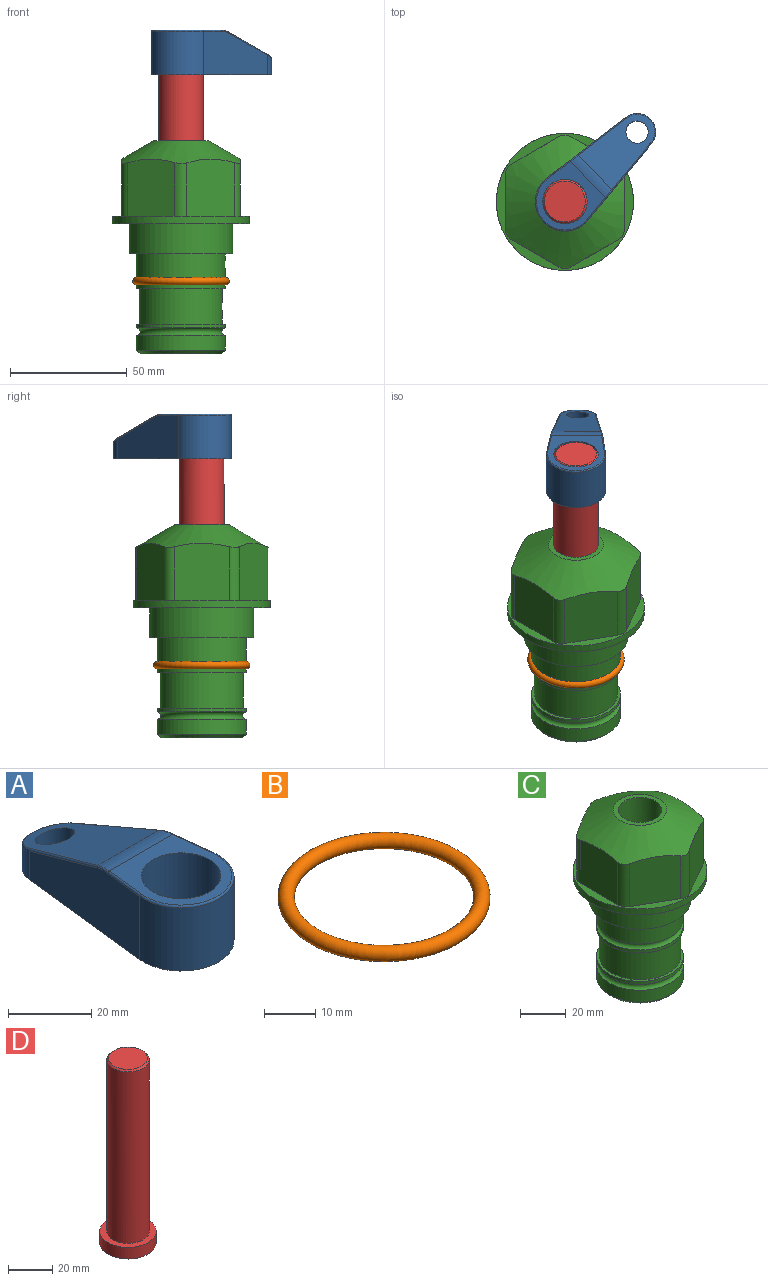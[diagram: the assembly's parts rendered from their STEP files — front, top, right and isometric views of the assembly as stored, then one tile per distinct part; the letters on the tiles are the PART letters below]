
ASSEMBLY  parts=4 mates=2
PART A: 44 faces, bbox 27.5x64.5x19.1 mm
  f0: plane 2.3x0.95mm, normal (0,0,-1), area 1mm2, adj f25,f30,f34
  f1: plane 63.5x25.4mm, normal (0,0,-1), area 561.7mm2, adj f2,f3,f4,f5,f6,f7,f19,f20
  f2: cylinder r=12.7mm len=25.4mm, axis (0,0,-1), area 792.2mm2, adj f1,f3,f5,f13
  f3: plane 42.33x18.54mm, normal (0.99,0.11,0), area 647mm2, adj f1,f2,f4,f11,f12,f14
  f4: cylinder r=7.94mm len=15.78mm, axis (0,0,-1), area 158.6mm2, adj f1,f3,f5,f16
  f5: plane 42.33x18.54mm, normal (-0.99,0.11,0), area 647mm2, adj f1,f2,f4,f15,f17,f18
  f6: cylinder r=9.53mm len=19.05mm, axis (0,0,-1), area 1140.1mm2, adj f1,f8
  f7: cylinder r=4.76mm len=10.98mm, axis (0,0,-1), area 276.1mm2, adj f1,f9
  f8: plane 25.83x24.38mm, normal (0,0,1), area 262.2mm2, adj f6,f10,f11,f13,f15
  f9: plane 32.49x20.55mm, normal (0,0.34,0.94), area 489.9mm2, adj f7,f10,f14,f16,f18
  f10: cylinder r=12.7mm len=21.49mm, axis (-1,0,0), area 93.2mm2, adj f8,f9,f12,f17
  f11: cylinder r=0.51mm len=12.34mm, axis (0.11,-0.99,0), area 9.9mm2, adj f3,f8,f12,f13
  f12: bspline ~7.62x1.64mm, area 3.5mm2, adj f3,f10,f11,f14
  f13: torus R=12.19mm, axis (0,0,1), area 33.6mm2, adj f2,f8,f11,f15
  f14: cylinder r=0.51mm len=26.01mm, axis (0.1,-0.93,0.34), area 21.6mm2, adj f3,f9,f12,f16
  f15: cylinder r=0.51mm len=12.34mm, axis (0.11,0.99,0), area 9.9mm2, adj f5,f8,f13,f17
  f16: bspline ~15.78x7.05mm, area 15.7mm2, adj f4,f9,f14,f18
  f17: bspline ~7.62x1.64mm, area 3.5mm2, adj f5,f10,f15,f18
  f18: cylinder r=0.51mm len=26.01mm, axis (0.1,0.93,-0.34), area 21.6mm2, adj f5,f9,f16,f17
  f19: plane 21.6x14.29mm, normal (-0.99,-0.11,0), area 242.6mm2, adj f1,f26,f28,f34,f36,f38
  f20: plane 21.6x14.29mm, normal (0.99,-0.11,0), area 242.6mm2, adj f1,f27,f29,f37,f39,f41
  f21: cylinder r=12.7mm len=14.29mm, axis (0,0,-1), area 173.2mm2, adj f1,f26,f27,f30,f31,f33
  f22: cylinder r=7.94mm len=7.63mm, axis (0,0,-1), area 53.8mm2, adj f1,f28,f29,f42
  f23: plane 2.3x0.95mm, normal (0,0,-1), area 1mm2, adj f25,f33,f37
  f24: plane 17.94x12.32mm, normal (0,-0.34,-0.94), area 191.2mm2, adj f25,f38,f41,f42
  f25: cylinder r=9.53mm len=12.93mm, axis (-1,0,0), area 37.5mm2, adj f0,f23,f24,f31,f36,f39
  f26: cylinder r=1.59mm len=14.29mm, axis (0,0,-1), area 49mm2, adj f1,f19,f21,f32
  f27: cylinder r=1.59mm len=14.29mm, axis (0,0,-1), area 49mm2, adj f1,f20,f21,f35
  f28: cylinder r=1.59mm len=7.28mm, axis (0,0,-1), area 22.1mm2, adj f1,f19,f22,f40
  f29: cylinder r=1.59mm len=7.28mm, axis (0,0,-1), area 22.1mm2, adj f1,f20,f22,f43
  f30: torus R=14.29mm, axis (0,0,1), area 5.8mm2, adj f0,f21,f31,f32
  f31: bspline ~11.06x2.73mm, area 20.8mm2, adj f21,f25,f30,f33
  f32: sphere r=1.59mm, area 5.4mm2, adj f26,f30,f34
  f33: torus R=14.29mm, axis (0,0,1), area 5.8mm2, adj f21,f23,f31,f35
  f34: cylinder r=1.59mm len=1.68mm, axis (-0.11,0.99,0), area 2.4mm2, adj f0,f19,f32,f36
  f35: sphere r=1.59mm, area 5.4mm2, adj f27,f33,f37
  f36: bspline ~5.82x2.33mm, area 7.7mm2, adj f19,f25,f34,f38
  f37: cylinder r=1.59mm len=1.68mm, axis (0.11,0.99,0), area 2.4mm2, adj f20,f23,f35,f39
  f38: cylinder r=1.59mm len=18.33mm, axis (0.1,-0.93,0.34), area 46.7mm2, adj f19,f24,f36,f40
  f39: bspline ~5.82x2.33mm, area 7.7mm2, adj f20,f25,f37,f41
  f40: sphere r=1.59mm, area 3.6mm2, adj f28,f38,f42
  f41: cylinder r=1.59mm len=18.33mm, axis (0.1,0.93,-0.34), area 46.7mm2, adj f20,f24,f39,f43
  f42: bspline ~8.31x1.84mm, area 15.3mm2, adj f22,f24,f40,f43
  f43: sphere r=1.59mm, area 3.6mm2, adj f29,f41,f42
PART B: 1 faces, bbox 44.7x44.7x3.2 mm
  f0: torus R=19.05mm, axis (0,0,1), area 1193.9mm2
PART C: 36 faces, bbox 58.7x58.7x91.2 mm
  f0: cylinder r=17.78mm len=35.56mm, axis (0,0,1), area 1670.8mm2, adj f23,f24,f31
  f1: cylinder r=19.05mm len=38.1mm, axis (0,0,1), area 1191.9mm2, adj f26,f27,f30
  f2: plane 58.66x58.66mm, normal (0,0,-1), area 1150.6mm2, adj f3,f28
  f3: cylinder r=29.33mm len=58.66mm, axis (0,0,-1), area 585.1mm2, adj f2,f4
  f4: plane 58.66x58.66mm, normal (0,0,1), area 475.9mm2, adj f3,f5,f6,f7,f8,f9,f10,f11
  f5: plane 24.5x20.32mm, normal (-0.5,0.87,0), area 562.8mm2, adj f4,f15,f16,f17
  f6: plane 24.5x20.32mm, normal (0.5,0.87,0), area 562.8mm2, adj f4,f14,f15,f17
  f7: plane 24.5x23.48mm, normal (1,0,0), area 562.8mm2, adj f4,f13,f14,f17
  f8: plane 24.5x20.32mm, normal (0.5,-0.87,0), area 562.8mm2, adj f4,f12,f13,f17
  f9: plane 24.5x20.32mm, normal (-0.5,-0.87,0), area 562.8mm2, adj f4,f11,f12,f17
  f10: plane 24.5x23.48mm, normal (-1,0,0), area 562.8mm2, adj f4,f11,f16,f17
  f11: cylinder r=5.08mm len=23.01mm, axis (0,0,-1), area 121.2mm2, adj f4,f9,f10,f17
  f12: cylinder r=5.08mm len=23.01mm, axis (0,0,-1), area 121.2mm2, adj f4,f8,f9,f17
  f13: cylinder r=5.08mm len=23.01mm, axis (0,0,-1), area 121.2mm2, adj f4,f7,f8,f17
  f14: cylinder r=5.08mm len=23.01mm, axis (0,0,-1), area 121.2mm2, adj f4,f6,f7,f17
  f15: cylinder r=5.08mm len=23.01mm, axis (0,0,-1), area 121.2mm2, adj f4,f5,f6,f17
  f16: cylinder r=5.08mm len=23.01mm, axis (0,0,-1), area 121.2mm2, adj f4,f5,f10,f17
  f17: cone r=11.73mm half-angle=60deg, axis (0,0,-1), area 2071.8mm2, adj f5,f6,f7,f8,f9,f10,f11,f12
  f18: plane 23.46x23.46mm, normal (0,0,1), area 147.4mm2, adj f17,f35
  f19: plane 34.93x34.93mm, normal (0,0,-1), area 958mm2, adj f29
  f20: cylinder r=19.05mm len=38.1mm, axis (0,0,1), area 760.1mm2, adj f21,f29
  f21: torus R=19.05mm, axis (0,0,1), area 565.3mm2, adj f20,f22
  f22: cylinder r=19.05mm len=38.1mm, axis (0,0,1), area 190mm2, adj f21,f23
  f23: plane 38.1x38.1mm, normal (0,0,1), area 146.9mm2, adj f0,f22
  f24: plane 38.1x38.1mm, normal (0,0,-1), area 146.9mm2, adj f0,f25
  f25: cylinder r=19.05mm len=38.1mm, axis (0,0,1), area 190mm2, adj f24,f26
  f26: torus R=19.05mm, axis (0,0,1), area 565.3mm2, adj f1,f25
  f27: plane 44.45x44.45mm, normal (0,0,-1), area 411.7mm2, adj f1,f28
  f28: cylinder r=22.23mm len=44.45mm, axis (0,0,1), area 1773.5mm2, adj f2,f27
  f29: cone r=19.05mm half-angle=45deg, axis (0,0,1), area 257.5mm2, adj f19,f20
  f30: cylinder r=3.17mm len=6.75mm, axis (-1,0,0), area 128mm2, adj f1,f33
  f31: cylinder r=3.17mm len=6.35mm, axis (-1,0,0), area 102.5mm2, adj f0,f33
  f32: plane 25.4x25.4mm, normal (0,0,1), area 506.7mm2, adj f33
  f33: cylinder r=12.7mm len=66.42mm, axis (0,0,-1), area 5236.2mm2, adj f30,f31,f32,f34
  f34: cone r=9.53mm half-angle=30deg, axis (0,0,-1), area 443.4mm2, adj f33,f35
  f35: cylinder r=9.53mm len=19.05mm, axis (0,0,-1), area 849mm2, adj f18,f34
PART D: 6 faces, bbox 25.4x25.4x101.6 mm
  f0: plane 17.46x17.46mm, normal (0,0,1), area 239.5mm2, adj f5
  f1: plane 25.4x25.4mm, normal (0,0,-1), area 506.7mm2, adj f2
  f2: cylinder r=12.7mm len=25.4mm, axis (0,0,1), area 506.7mm2, adj f1,f3
  f3: plane 25.4x25.4mm, normal (0,0,1), area 221.7mm2, adj f2,f4
  f4: cylinder r=9.53mm len=94.46mm, axis (0,0,1), area 5653mm2, adj f3,f5
  f5: cone r=8.73mm half-angle=45deg, axis (0,0,-1), area 64.4mm2, adj f0,f4
PLACE A rot(axis=(0,0,-1),46.1deg) t=(0,0,63.85)mm
PLACE B at identity
PLACE C at identity fixed
PLACE D rot(axis=(0,0,-1),46.1deg) t=(0,0,9.24)mm
MATE cylindrical D.f2 <-> C.f0  axis (0,0,1) through (0,0,34.88)mm
MATE fastened A.f2 <-> D.f2  axis (0,0,-1) through (0,0,82.9)mm
